# Revit family: CENTUM Festpunkt Typ B m XL100 Massivanschluss, Gummi
name_source: partatom
category: HLS-Bauteile
revit_build: Autodesk Revit 2017 (Build: 20190507_1515(x64)
units: mm (PartAtom-declared; Revit-internal decimal feet)

## family parameters
Arbeitsebenenbasiert = Ja
Beim Laden mit Abzugskörper schneiden = Nein
Bemaßung runder Anschluss = Durchmesser verwenden
Gemeinsam genutzt = Ja
Immer vertikal = Nein
Raumberechnungspunkt = Nein
Teiletyp = Normal

## types (4) — shared parameters
AB = 5 mm  [stored 0.0164042 ft]
Anzahl Rohrschellen = 2
Aufbaumaß = 69 mm
Ausführung = CENTUM Massivanschluss
Breite Material Rohrschelle = 50 mm
Breite Profilstahl = 65 mm
Druckstück = Druckstück Typ II Gummi
Fabrikat = MEFA
Firma = MEFA Befestigungs- und Montagesysteme GmbH
Höhe Profilstahl = 42 mm
Klammergröße = 2
Kurztext1 = Festpunkt Typ B
Länge Druckstück = 116 mm
Länge Profilstahl = 200 mm  [stored 0.656168 ft]
Material Druckstücke = Stahl
Material Schalldämmeinlage = TPE/EPDM
Materialname Druckstücke = S235JR
Mengeneinheit = St
Oberfläche Druckstücke = blank
Oberfläche Träger + Schellen = galvanisch verzinkt
Profilstahltyp = U65
Rohrschellentyp = Titan HD
Schalldämmeinlage = Gummi
Stärke Material Rohrschelle = 5 mm
Vorgabe-Ansicht = 1219 mm
max. Temperaturbeständigkeit = 100 °C
vpe = 1 St
zero-valued in all types: max. Höhe, max. Rohraußendurchmesser, min. Rohraußendurchmesser

## per-type parameters (varying)
| type | Artikelnummer | Breite | EAN | Gewicht | Gewicht pro Bauteil | Kurztext2 | RA | Rohraußendurchmesser | Rohrschellen | max. Axiale Reaktionskraft |
| CENTUM Festpunkt Typ B, Ø 60,3, m. XL100 Massivanschluss, Gummi | 9993378 | 148 mm  [stored 0.485564 ft] | 4250928454249 | 10.50 kg | 10.50 kg | 60,3 mm Gummi CENTUM Massivanschl. | 73 mm  [stored 0.239501 ft] | 60 mm  [stored 0.19685 ft] | MEFA RS Titan HD, Ø60,3-Ø160 mm, TPE : MEFA RS Titan HD, Ø60,3 mm, TPE |  |
| CENTUM Festpunkt Typ B, Ø 76,1, m. XL100 Massivanschluss, Gummi | 9991592 | 166 mm  [stored 0.544619 ft] | 4250928454256 | 10.74 kg | 10.74 kg | 76,1 mm Gummi CENTUM Massivanschl. | 84 mm  [stored 0.275591 ft] | 76 mm  [stored 0.249344 ft] | MEFA RS Titan HD, Ø60,3-Ø160 mm, TPE : MEFA RS Titan HD, Ø76,1mm, TPE |  |
| CENTUM Festpunkt Typ B, Ø 88,9, m. XL100 Massivanschluss, Gummi | 9991611 | 179 mm  [stored 0.58727 ft] | 4250928454263 | 10.94 kg | 10.94 kg | 88,9 mm Gummi CENTUM Massivanschl. | 91 mm  [stored 0.298556 ft] | 89 mm | MEFA RS Titan HD, Ø60,3-Ø160 mm, TPE : MEFA RS Titan HD, Ø88,9 mm, AG M12, TPE |  |
| CENTUM Festpunkt Typ B, Ø114,3, m. XL100 Massivanschluss, Gummi | 9992192 | 205 mm  [stored 0.672572 ft] | 4250928454270 | 11.31 kg | 11.31 kg | 114,3 mm Gummi CENTUM Massivanschl. | 105 mm  [stored 0.344488 ft] | 114 mm  [stored 0.374016 ft] | MEFA RS Titan HD, Ø60,3-Ø160 mm, TPE : MEFA RS Titan HD, Ø114,3 mm, TPE | 40 kN |

note: [stored X ft] marks values corroborated as IEEE doubles in the binary element streams (Revit-internal decimal feet)

## geometry (parser evidence)
native form markers: Sweep x6
no freeform markers — native parametric forms only
